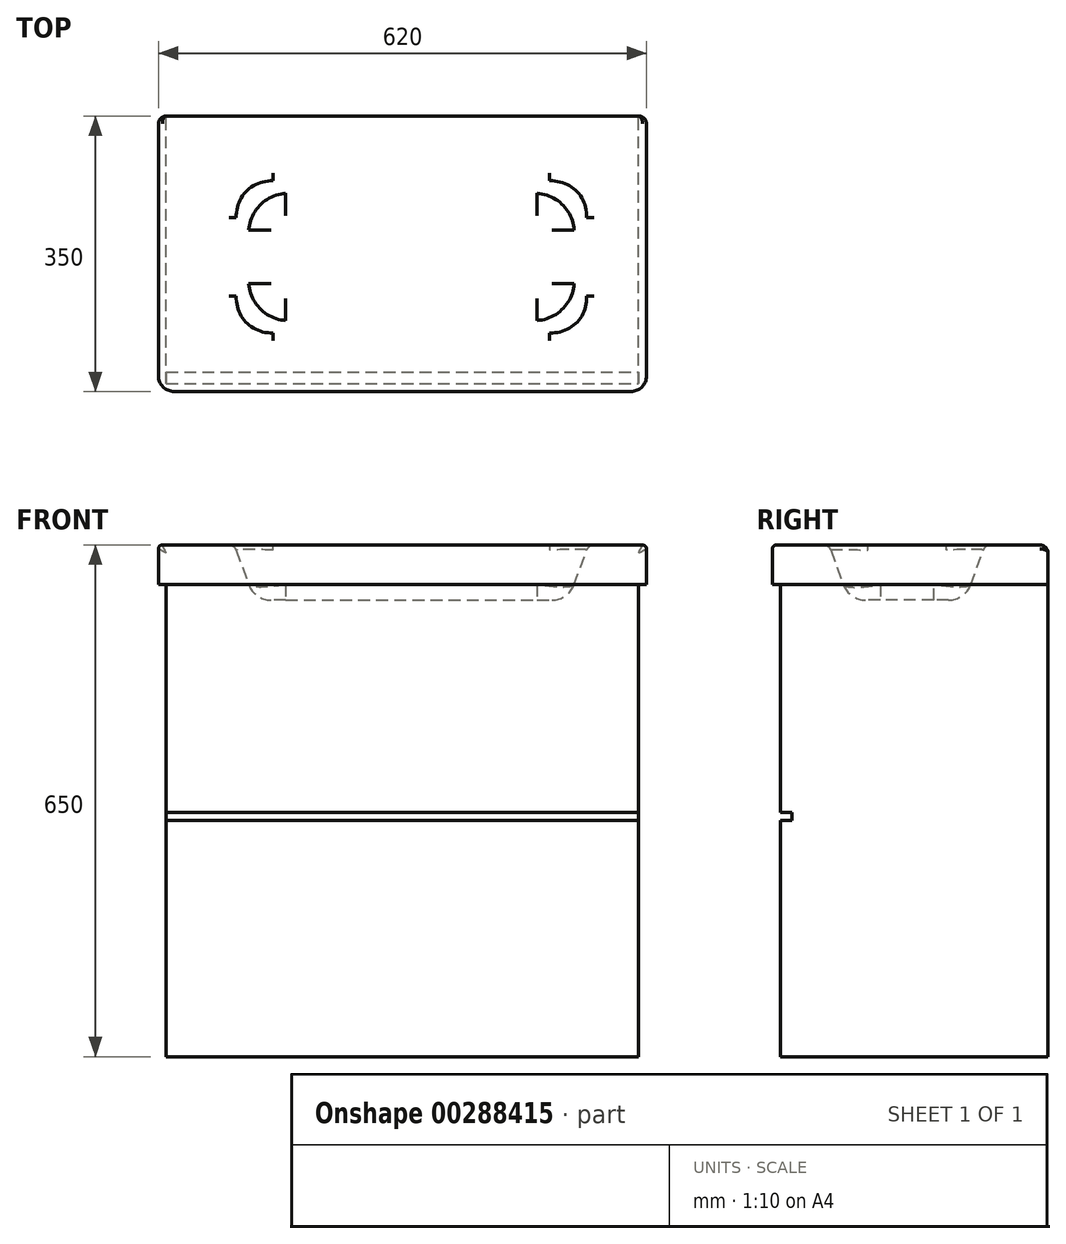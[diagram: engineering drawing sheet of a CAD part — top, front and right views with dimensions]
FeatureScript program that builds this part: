
annotation { "Feature Type Name" : "Feature", "Feature Type Description" : "" }
export const myFeature = defineFeature(function(context is Context, id is Id, definition is map)
    precondition{}
    {
        {
            var Q0;
            Q0=qCreatedBy(makeId("Front.planeOp"),FACE);
            var sketch = newSketch(context, id + "F0", { "sketchPlane" : qUnion([Q0])});
            skLineSegment(sketch, "E0.bottom", {"start": v(0, 0) * mm, "end": v(600, 0) * mm});
            skLineSegment(sketch, "E0.top", {"start": v(0, 600) * mm, "end": v(600, 600) * mm});
            skLineSegment(sketch, "E0.left", {"start": v(0, 0) * mm, "end": v(0, 600) * mm});
            skLineSegment(sketch, "E0.right", {"start": v(600, 0) * mm, "end": v(600, 600) * mm});
            skSolve(sketch);
        }
        {
            var Q0;
            Q0 = qSketchRegion(id + "F0", true);
            extrude(context, id + "F1", {"entities" : qUnion([Q0]), "depth" : 340 * mm});
        }
        {
            var Q0;
            Q0=makeQuery(id+"F1.opExtrude","CAP_FACE",FACE,{"disambiguationData":[OSD([sQuery(id+"F0.wireOp",EDGE,"E0.bottom"),sQuery(id+"F0.wireOp",EDGE,"E0.top"),sQuery(id+"F0.wireOp",EDGE,"E0.left"),sQuery(id+"F0.wireOp",EDGE,"E0.right")])],"isStart":false});
            var sketch = newSketch(context, id + "F2", { "sketchPlane" : qUnion([Q0])});
            skLineSegment(sketch, "E1.bottom", {"start": v(-30, 300) * mm, "end": v(620, 300) * mm});
            skLineSegment(sketch, "E1.top", {"start": v(-30, 310) * mm, "end": v(620, 310) * mm});
            skLineSegment(sketch, "E1.left", {"start": v(-30, 300) * mm, "end": v(-30, 310) * mm});
            skLineSegment(sketch, "E1.right", {"start": v(620, 300) * mm, "end": v(620, 310) * mm});
            skSolve(sketch);
        }
        {
            var Q0;
            {var subQ0=sQuery(id+"F2.wireOp",EDGE,"E1.bottom");var subQ1=makeQuery(id+"F1.opExtrude","CAP_EDGE",EDGE,{"disambiguationData":[OSD([sQuery(id+"F0.wireOp",EDGE,"E0.left")])],"isStart":false});var subQ2=makeQuery(id+"F2.imprint","INTERSECT",VERTEX,{"derivedFrom":[subQ1,subQ0]});Q0=makeQuery(id+"F2.imprint","IMPRINT",FACE,{"disambiguationData":[TD([[makeQuery(id+"F2.imprint","IMPRINT",EDGE,{"disambiguationData":[TD([[subQ2,-1.0]])],"derivedFrom":subQ0}),1.0]])]});}
            var Q1;
            {var subQ0=sQuery(id+"F2.wireOp",EDGE,"E1.left");Q1=makeQuery(id+"F2.imprint","IMPRINT",FACE,{"disambiguationData":[TD([[makeQuery(id+"F2.imprint","IMPRINT",EDGE,{"derivedFrom":subQ0}),-1.0]])]});}
            var Q2;
            {var subQ0=sQuery(id+"F2.wireOp",EDGE,"E1.right");Q2=makeQuery(id+"F2.imprint","IMPRINT",FACE,{"disambiguationData":[TD([[makeQuery(id+"F2.imprint","IMPRINT",EDGE,{"derivedFrom":subQ0}),1.0]])]});}
            extrude(context, id + "F3", {"entities" : qUnion([Q0, Q1, Q2]), "operationType" : NewBodyOperationType.REMOVE, "oppositeDirection" : true, "depth" : 15 * mm});
        }
        {
            var Q0;
            Q0=makeQuery(id+"F1.opExtrude","SWEPT_FACE",FACE,{"disambiguationData":[OSD([sQuery(id+"F0.wireOp",EDGE,"E0.top")])]});
            var sketch = newSketch(context, id + "F4", { "sketchPlane" : qUnion([Q0])});
            skLineSegment(sketch, "E2.bottom", {"start": v(-10, 0) * mm, "end": v(610, 0) * mm});
            skLineSegment(sketch, "E2.top", {"start": v(-10, -350) * mm, "end": v(610, -350) * mm});
            skLineSegment(sketch, "E2.left", {"start": v(-10, 0) * mm, "end": v(-10, -350) * mm});
            skLineSegment(sketch, "E2.right", {"start": v(610, 0) * mm, "end": v(610, -350) * mm});
            skSolve(sketch);
        }
        {
            var Q0;
            Q0 = qSketchRegion(id + "F4", true);
            extrude(context, id + "F5", {"entities" : qUnion([Q0]), "operationType" : NewBodyOperationType.ADD, "depth" : 50 * mm});
        }
        {
            var Q0;
            Q0=makeQuery(id+"F5.opExtrude","SWEPT_EDGE",EDGE,{"disambiguationData":[OSD([sQuery(id+"F4.wireOp",EDGE,"E2.top"),sQuery(id+"F4.wireOp",EDGE,"E2.left")])]});
            var Q1;
            Q1=makeQuery(id+"F5.opExtrude","SWEPT_EDGE",EDGE,{"disambiguationData":[OSD([sQuery(id+"F4.wireOp",EDGE,"E2.top"),sQuery(id+"F4.wireOp",EDGE,"E2.right")])]});
            fillet(context, id + "F6", {"entities" : qUnion([Q0, Q1]), "radius" : 20 * mm, "tangentPropagation" : true, "allowEdgeOverflow" : false});
        }
        {
            var Q0;
            Q0=makeQuery(id+"F5.opExtrude","CAP_EDGE",EDGE,{"disambiguationData":[OSD([sQuery(id+"F4.wireOp",EDGE,"E2.top")])],"isStart":false});
            var Q1;
            {var subQ0=sQuery(id+"F4.wireOp",EDGE,"E2.left");var subQ1=sQuery(id+"F4.wireOp",EDGE,"E2.top");Q1=makeQuery(id+"F6.opFillet","BLEND_EDGE",EDGE,{"blendedFrom":[makeQuery(id+"F5.opExtrude","SWEPT_EDGE",EDGE,{"disambiguationData":[OSD([subQ1,subQ0])]}),makeQuery(id+"F5.opExtrude","CAP_FACE",FACE,{"disambiguationData":[OSD([sQuery(id+"F4.wireOp",EDGE,"E2.bottom"),subQ1,subQ0,sQuery(id+"F4.wireOp",EDGE,"E2.right")])],"isStart":false})],"blendedInto":[makeQuery(id+"F5.opExtrude","CAP_FACE",FACE,{"disambiguationData":[OSD([sQuery(id+"F4.wireOp",EDGE,"E2.bottom"),subQ1,subQ0,sQuery(id+"F4.wireOp",EDGE,"E2.right")])],"isStart":false})]});}
            var Q2;
            Q2=makeQuery(id+"F5.opExtrude","CAP_EDGE",EDGE,{"disambiguationData":[OSD([sQuery(id+"F4.wireOp",EDGE,"E2.left")])],"isStart":false});
            var Q3;
            Q3=makeQuery(id+"F5.opExtrude","CAP_EDGE",EDGE,{"disambiguationData":[OSD([sQuery(id+"F4.wireOp",EDGE,"E2.right")])],"isStart":false});
            var Q4;
            {var subQ0=sQuery(id+"F4.wireOp",EDGE,"E2.right");var subQ1=sQuery(id+"F4.wireOp",EDGE,"E2.top");Q4=makeQuery(id+"F6.opFillet","BLEND_EDGE",EDGE,{"blendedFrom":[makeQuery(id+"F5.opExtrude","SWEPT_EDGE",EDGE,{"disambiguationData":[OSD([subQ1,subQ0])]}),makeQuery(id+"F5.opExtrude","CAP_FACE",FACE,{"disambiguationData":[OSD([sQuery(id+"F4.wireOp",EDGE,"E2.bottom"),subQ1,sQuery(id+"F4.wireOp",EDGE,"E2.left"),subQ0])],"isStart":false})],"blendedInto":[makeQuery(id+"F5.opExtrude","CAP_FACE",FACE,{"disambiguationData":[OSD([sQuery(id+"F4.wireOp",EDGE,"E2.bottom"),subQ1,sQuery(id+"F4.wireOp",EDGE,"E2.left"),subQ0])],"isStart":false})]});}
            fillet(context, id + "F7", {"entities" : qUnion([Q0, Q1, Q2, Q3, Q4]), "radius" : 5 * mm, "tangentPropagation" : true, "allowEdgeOverflow" : false});
        }
        {
            var Q0;
            Q0=makeQuery(id+"F5.opExtrude","CAP_FACE",FACE,{"disambiguationData":[OSD([sQuery(id+"F4.wireOp",EDGE,"E2.bottom"),sQuery(id+"F4.wireOp",EDGE,"E2.top"),sQuery(id+"F4.wireOp",EDGE,"E2.left"),sQuery(id+"F4.wireOp",EDGE,"E2.right")])],"isStart":false});
            var sketch = newSketch(context, id + "F8", { "sketchPlane" : qUnion([Q0])});
            skLineSegment(sketch, "E3.bottom", {"start": v(86.46, -278.16) * mm, "end": v(536.46, -278.16) * mm});
            skLineSegment(sketch, "E3.top", {"start": v(86.46, -79.84) * mm, "end": v(536.46, -79.84) * mm});
            skLineSegment(sketch, "E3.left", {"start": v(86.46, -278.16) * mm, "end": v(86.46, -79.84) * mm});
            skLineSegment(sketch, "E3.right", {"start": v(536.46, -278.16) * mm, "end": v(536.46, -79.84) * mm});
            skSolve(sketch);
        }
        {
            var Q0;
            Q0 = qSketchRegion(id + "F8", true);
            extrude(context, id + "F9", {"entities" : qUnion([Q0]), "operationType" : NewBodyOperationType.REMOVE, "oppositeDirection" : true, "depth" : 70 * mm, "hasDraft" : true, "draftAngle" : 20 * degree, "draftPullDirection" : true});
        }
        {
            var Q0;
            Q0=makeQuery(id+"F9.boolean.opBoolean","COPY",EDGE,{"derivedFrom":makeQuery(id+"F9.opExtrude","SWEPT_EDGE",EDGE,{"disambiguationData":[OSD([sQuery(id+"F8.wireOp",EDGE,"E3.top"),sQuery(id+"F8.wireOp",EDGE,"E3.left")])]})});
            var Q1;
            Q1=makeQuery(id+"F9.boolean.opBoolean","COPY",EDGE,{"derivedFrom":makeQuery(id+"F9.opExtrude","SWEPT_EDGE",EDGE,{"disambiguationData":[OSD([sQuery(id+"F8.wireOp",EDGE,"E3.top"),sQuery(id+"F8.wireOp",EDGE,"E3.right")])]})});
            var Q2;
            Q2=makeQuery(id+"F9.boolean.opBoolean","COPY",EDGE,{"derivedFrom":makeQuery(id+"F9.opExtrude","SWEPT_EDGE",EDGE,{"disambiguationData":[OSD([sQuery(id+"F8.wireOp",EDGE,"E3.bottom"),sQuery(id+"F8.wireOp",EDGE,"E3.right")])]})});
            var Q3;
            Q3=makeQuery(id+"F9.boolean.opBoolean","COPY",EDGE,{"derivedFrom":makeQuery(id+"F9.opExtrude","SWEPT_EDGE",EDGE,{"disambiguationData":[OSD([sQuery(id+"F8.wireOp",EDGE,"E3.bottom"),sQuery(id+"F8.wireOp",EDGE,"E3.left")])]})});
            fillet(context, id + "F10", {"entities" : qUnion([Q0, Q1, Q2, Q3]), "radius" : 50 * mm, "tangentPropagation" : true, "allowEdgeOverflow" : false});
        }
        {
            var Q0;
            Q0=makeQuery(id+"F9.boolean.opBoolean","COPY",FACE,{"derivedFrom":makeQuery(id+"F9.opExtrude","CAP_FACE",FACE,{"disambiguationData":[OSD([sQuery(id+"F8.wireOp",EDGE,"E3.bottom"),sQuery(id+"F8.wireOp",EDGE,"E3.top"),sQuery(id+"F8.wireOp",EDGE,"E3.left"),sQuery(id+"F8.wireOp",EDGE,"E3.right")])],"isStart":false})});
            fillet(context, id + "F11", {"entities" : qUnion([Q0]), "radius" : 30 * mm, "tangentPropagation" : true, "allowEdgeOverflow" : false});
        }
        {
            var Q0;
            Q0=makeQuery(id+"F5.opExtrude","CAP_FACE",FACE,{"disambiguationData":[OSD([sQuery(id+"F4.wireOp",EDGE,"E2.bottom"),sQuery(id+"F4.wireOp",EDGE,"E2.top"),sQuery(id+"F4.wireOp",EDGE,"E2.left"),sQuery(id+"F4.wireOp",EDGE,"E2.right")])],"isStart":false});
            fillet(context, id + "F12", {"entities" : qUnion([Q0]), "radius" : 10 * mm, "tangentPropagation" : true, "allowEdgeOverflow" : false});
        }
    });
